# Revit family: FU_Modular_Sandler_Chanel 5559
name_source: partatom
category: Furniture
units: mm (PartAtom-declared; Revit-internal decimal feet)

## family parameters
Always vertical = Yes
Cut with Voids When Loaded = No
OmniClass Number = 23.40.20.00
OmniClass Title = General Furniture and Specialties
Render Appearance Source = Family Geometry
Room Calculation Point = No
Shared = No
Work Plane-Based = No

## types (1)
- Chanel 5559
    Default Elevation = 0 mm  [stored 0 ft]
    Depth = 930 mm  [stored 3.05118 ft]
    Description = Modular, trapezoidal seat with a convex curve. Can be part of a Chanel sectional sofa or used as a freestanding unit. Solid wood inner frame and comfortable webbed seat.
    Height = 790 mm  [stored 2.59186 ft]
    Manufacturer = Sandler
    Model = Chanel 5559
    URL = https://www.sandlerseating.com
    Width = 1250 mm  [stored 4.10105 ft]

note: [stored X ft] marks values corroborated as IEEE doubles in the binary element streams (Revit-internal decimal feet)

## geometry (parser evidence)
native form markers: Sweep x4
no freeform markers — native parametric forms only
